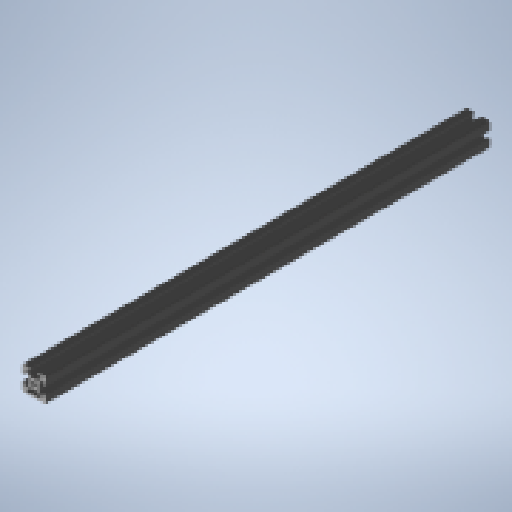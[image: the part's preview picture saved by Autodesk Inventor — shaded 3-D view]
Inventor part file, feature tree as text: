
AUTODESK INVENTOR PART (.ipt)
format: ipt  version: 2024 (Build 280153000, 153)  size: 368,128 bytes
history: native  units: mm
features: other x7, thread x2, sketch x2, extrude x1, hole x1
ambient origin geometry x8: Origin, YZ Plane, XZ Plane, XY Plane, X Axis, Y Axis, Z Axis, Center Point
bodies: Solid1 (feature_tree)
feature tree (13):
  extrude  "Extrusion1"  TaperAngle=0.0deg  [1 undecoded]
  hole  "Hole1"  [1 undecoded]
  other  "C1_XY"
  other  "C1_YZ"
  other  "C1_ZX"
  other  "C1_X"
  other  "C1_Y"
  other  "C1_Z"
  other  "C1_Center"
  thread  "Thread1"  [1 undecoded]
  thread  "Thread2"  [1 undecoded]
  sketch  "Sketch_63"  dims[d2=4.2mm d3=6.0mm d4=4.0mm d5=2.0mm d6=90.0deg d7=440.0mm d8=0.0mm d9=0.0mm d10=10.0mm d11=0.0mm d12=10.0mm d13=0.0mm]
  sketch  "Sketch2"  dims[d0=375.0mm d1=0.0mm]
note: 4 required parameter values undecoded (feature->parameter linkage not recoverable at this tier; creation-order binding heuristic only, values carry confidence <= 0.55)
